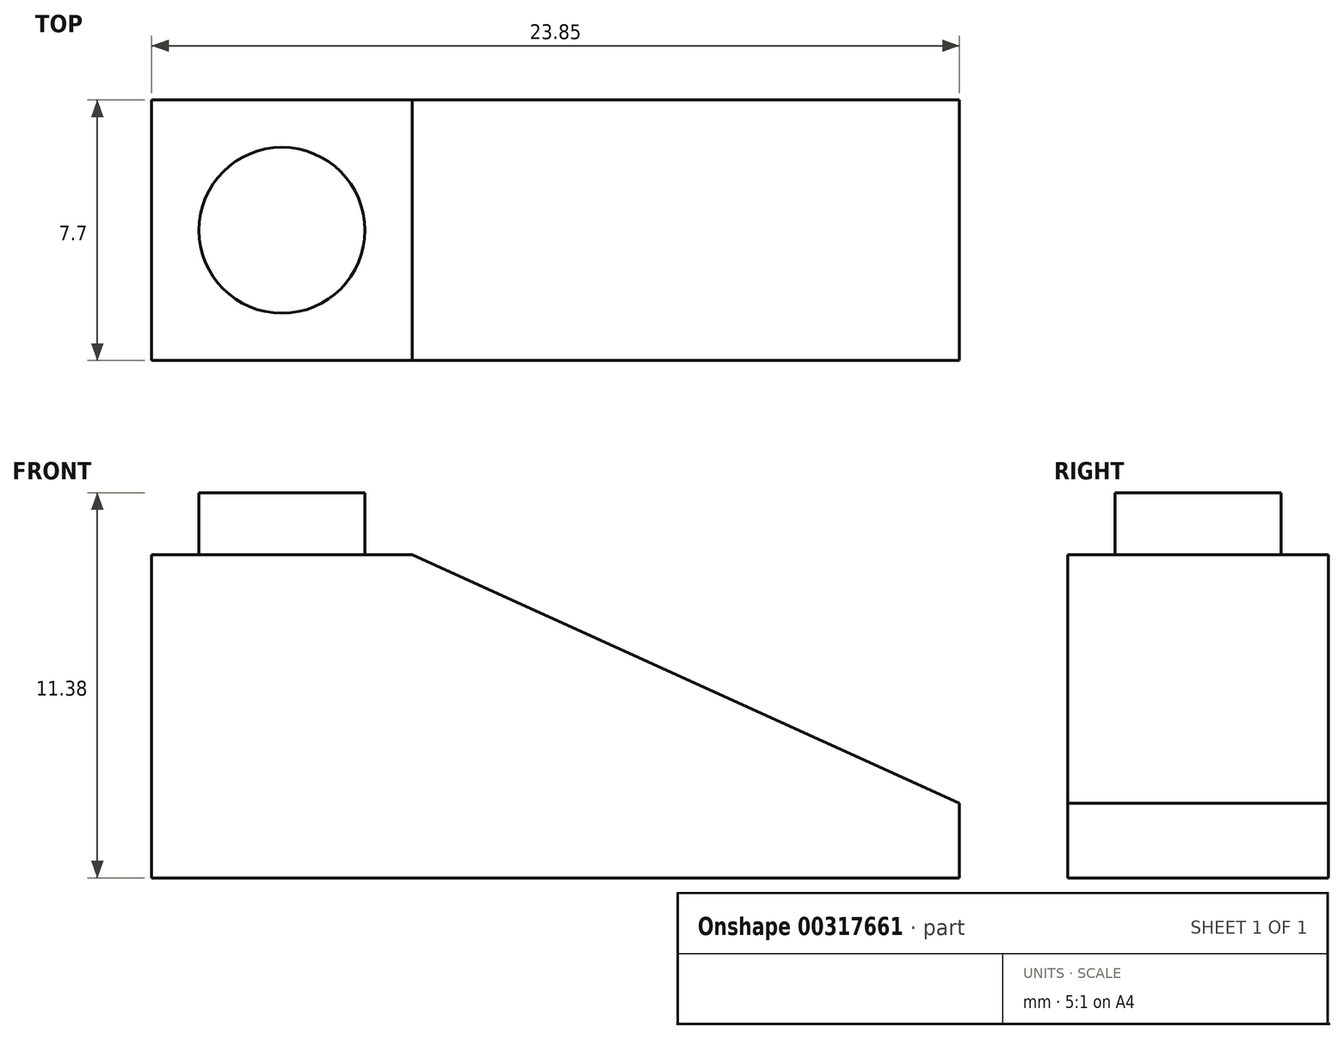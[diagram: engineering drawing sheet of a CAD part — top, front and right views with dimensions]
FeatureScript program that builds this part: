
annotation { "Feature Type Name" : "Feature", "Feature Type Description" : "" }
export const myFeature = defineFeature(function(context is Context, id is Id, definition is map)
    precondition{}
    {
        {
            var Q0;
            Q0=qCreatedBy(makeId("Front.planeOp"),FACE);
            var sketch = newSketch(context, id + "F0", { "sketchPlane" : qUnion([Q0])});
            skLineSegment(sketch, "E0", {"start": v(0, 9.55) * mm, "end": v(7.7, 9.55) * mm});
            skLineSegment(sketch, "E1", {"start": v(7.7, 9.55) * mm, "end": v(7.7, 0) * mm});
            skLineSegment(sketch, "E2", {"start": v(7.7, 0) * mm, "end": v(0, 0) * mm});
            skLineSegment(sketch, "E3", {"start": v(0, 0) * mm, "end": v(0, 9.55) * mm});
            skLineSegment(sketch, "E4", {"start": v(7.7, 9.55) * mm, "end": v(23.85, 2.2) * mm});
            skLineSegment(sketch, "E5", {"start": v(23.85, 2.2) * mm, "end": v(23.85, 0) * mm});
            skLineSegment(sketch, "E6", {"start": v(23.85, 0) * mm, "end": v(7.7, 0) * mm});
            skSolve(sketch);
        }
        {
            var Q0;
            Q0 = qSketchRegion(id + "F0", true);
            extrude(context, id + "F1", {"entities" : qUnion([Q0]), "depth" : 7.7 * mm});
        }
        {
            var Q0;
            Q0=makeQuery(id+"F1.opExtrude","SWEPT_FACE",FACE,{"disambiguationData":[OSD([sQuery(id+"F0.wireOp",EDGE,"E0")])]});
            var sketch = newSketch(context, id + "F2", { "sketchPlane" : qUnion([Q0])});
            skCircle(sketch, "E7", {"center": v(3.85, -3.85) * mm, "radius": 2.45 * mm});
            skPoint(sketch, "E7.centerSnap0", {"position": v(7.7, -3.85) * mm});
            skPoint(sketch, "E7.centerSnap1", {"position": v(3.85, 0) * mm});
            skSolve(sketch);
        }
        {
            var Q0;
            Q0=makeQuery(id+"F2.imprint","IMPRINT",FACE,{"disambiguationData":[TD([[makeQuery(id+"F2.imprint","IMPRINT",EDGE,{"derivedFrom":sQuery(id+"F2.wireOp",EDGE,"E7")}),1.0]])]});
            extrude(context, id + "F3", {"entities" : qUnion([Q0]), "operationType" : NewBodyOperationType.ADD, "depth" : 1.83 * mm});
        }
    });
